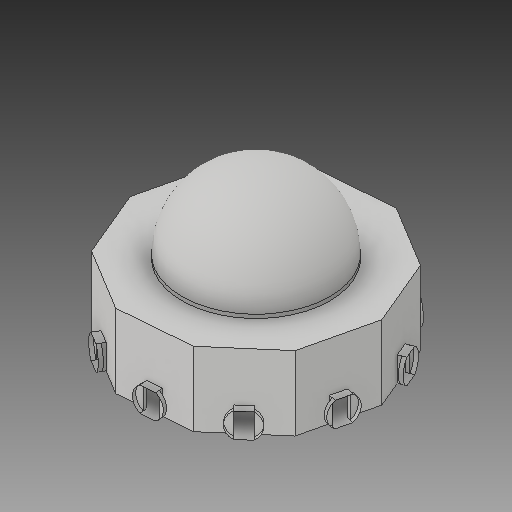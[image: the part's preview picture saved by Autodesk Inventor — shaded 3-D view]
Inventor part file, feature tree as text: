
AUTODESK INVENTOR PART (.ipt)
format: ipt  version: 2017 (Build 210142000, 142)  size: 340,480 bytes
history: native  units: in
note: dims shown in document units (in); Inventor stores cm internally (conversion verified against a paired STEP export)
features: extrude x5, sketch x5, other x2, pattern_circular x1, delete_face x1
ambient origin geometry x8: Origin, YZ Plane, XZ Plane, XY Plane, X Axis, Y Axis, Z Axis, Center Point
bodies: Solid1 (feature_tree)
feature tree (14):
  extrude  "bace"  Depth=1.0in TaperAngle=0.0deg
  extrude  "bace wall"  Depth=20.0in TaperAngle=0.0deg
  extrude  "bace cieiling"  Depth=6.6667in
  other  "dome work plane"
  other  "dome"
  extrude  "door frame"  Depth=1.0in
  extrude  "corridor connect"  Depth=21.0in
  pattern_circular  "Circular Pattern1"  Angle=90.0deg  [1 undecoded]
  delete_face  "Delete Face2"
  sketch  "Sketch1"  dims[d0=62.0in d1=1.0in d2=0.0in]
  sketch  "Sketch2"  dims[d4=1.0in d5=20.0in d6=0.0in]
  sketch  "Sketch3"  dims[d8=1.0in d9=0.0in d16=2.0in d17=6.6667in]
  sketch  "Sketch8"  dims[d18=1.0in d19=0.0in d28=40.0in]
  sketch  "Sketch10"  dims[d32=20.0in d33=21.0in d34=90.0deg d35=3.937in d36=360.0deg d74=4.0in d76=3.8873in d77=3.8873in d81=1.6458in d86=3.3333in d87=1.0in d90=1.0in d91=1.0in d92=0.0in]
note: 1 required parameter value undecoded (feature->parameter linkage not recoverable at this tier; creation-order binding heuristic only, values carry confidence <= 0.55)
